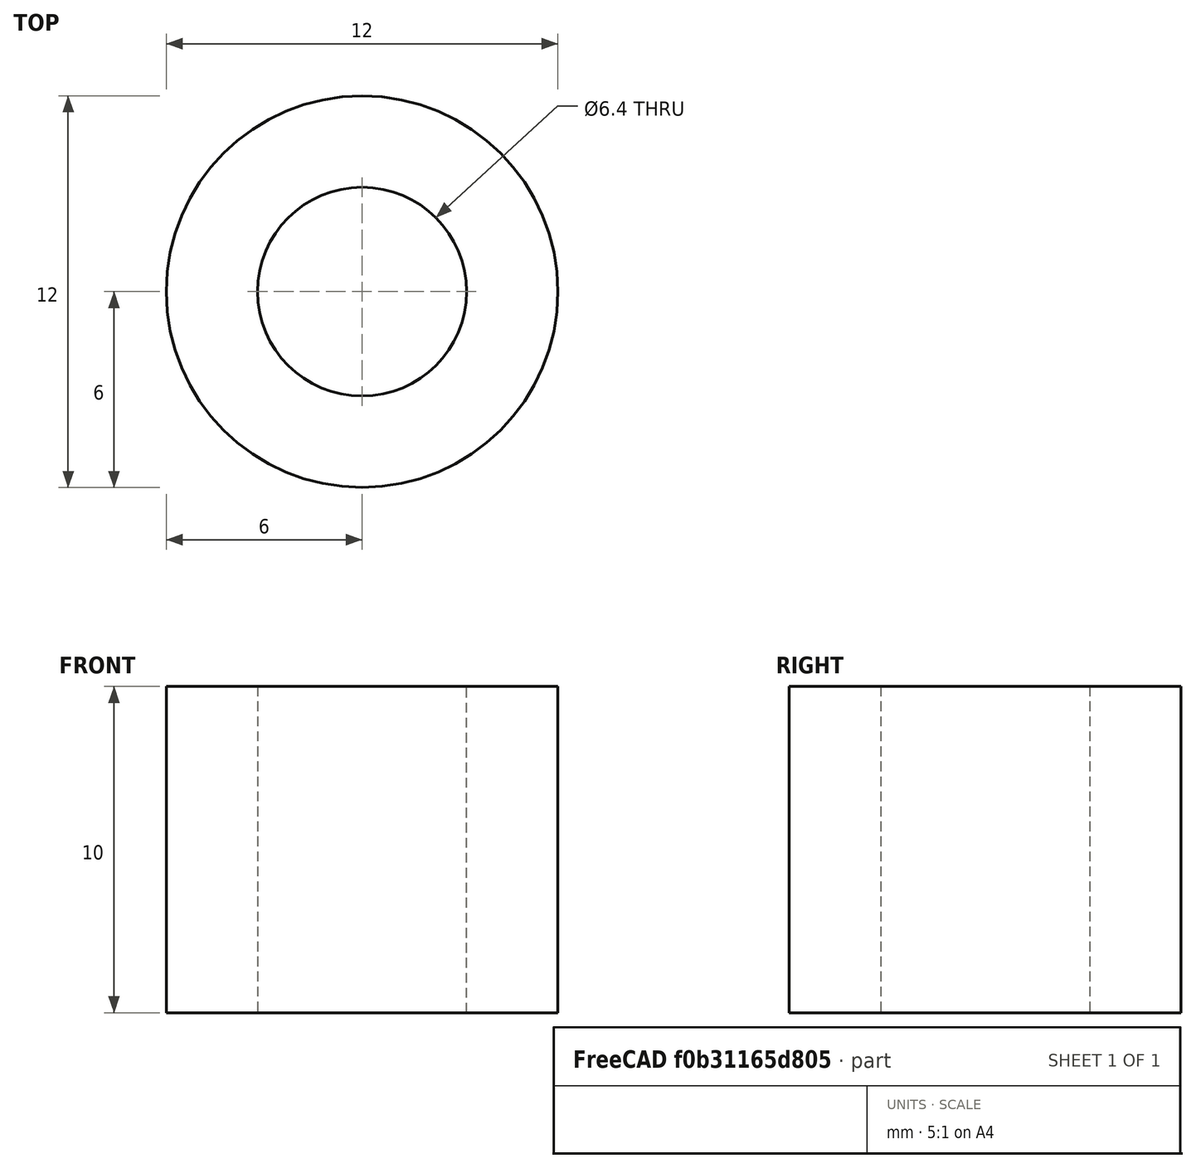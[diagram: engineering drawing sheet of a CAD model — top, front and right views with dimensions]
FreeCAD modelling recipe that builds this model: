
FCSTD DOCUMENT  (FreeCAD 0.17R8073 (Git))
Label: 10mm_M5_thumbscrew_spacer
License: CreativeCommons Attribution-ShareAlike
LicenseURL: http://creativecommons.org/licenses/by-sa/4.0/
objects: Sketcher::SketchObject×1, PartDesign::Pad×1, PartDesign::Body×1
note: 4 computed .brp shape members not serialized (recipe doc carries the construction recipe); baked Part::Feature solids carry a one-line shape summary decoded from their .brp

FEATURE [Sketcher::SketchObject] Sketch
  MapMode = 5
  Support = -> [XY_Plane]
  sketch-geometry (2):
    g0: Circle CenterX=0 CenterY=0 CenterZ=0 NormalX=0 NormalY=0 NormalZ=1 Radius=6
    g1: Circle CenterX=0 CenterY=0 CenterZ=0 NormalX=0 NormalY=0 NormalZ=1 Radius=3.2
  constraints (4):
    c: Coincident(g0,g-1)
    c: Radius(g0) = 6
    c: Coincident(g0,g1)
    c: Radius(g1) = 3.2
FEATURE [PartDesign::Pad] Pad
  Length = 10
  Length2 = 100
  Profile = -> Sketch
  Type = 0
FEATURE [PartDesign::Body] Body
  Model = -> [Sketch,Pad]
  Origin = -> BodyOrigin
  Tip = -> Pad
